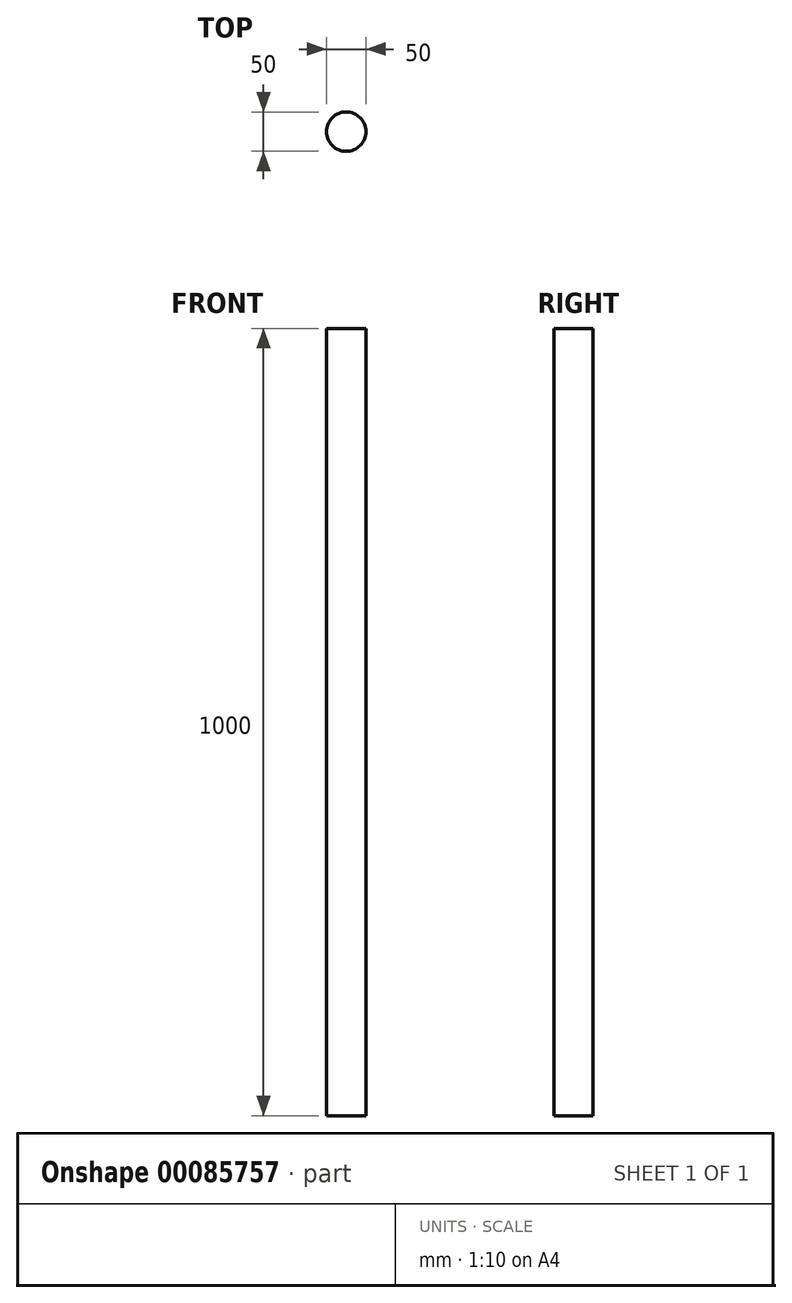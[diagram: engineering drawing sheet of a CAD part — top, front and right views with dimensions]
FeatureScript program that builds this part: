
annotation { "Feature Type Name" : "Feature", "Feature Type Description" : "" }
export const myFeature = defineFeature(function(context is Context, id is Id, definition is map)
    precondition{}
    {
        {
            var Q0;
            Q0=qCreatedBy(makeId("Top.planeOp"),FACE);
            var sketch = newSketch(context, id + "F0", { "sketchPlane" : qUnion([Q0])});
            skCircle(sketch, "E0", {"center": v(0, 0) * mm, "radius": 25 * mm});
            skSolve(sketch);
        }
        {
            var Q0;
            Q0=makeQuery(id+"F0.imprint","IMPRINT",FACE,{"disambiguationData":[TD([[makeQuery(id+"F0.imprint","IMPRINT",EDGE,{"derivedFrom":sQuery(id+"F0.wireOp",EDGE,"E0")}),1.0]])]});
            extrude(context, id + "F1", {"entities" : qUnion([Q0]), "depth" : 1000 * mm});
        }
    });
